FCSTD DOCUMENT  (FreeCAD 0.19R18524 (Git))
Label: footprint-RF-antenna-w-solder-Mask
License: All rights reserved
LicenseURL: http://en.wikipedia.org/wiki/All_rights_reserved
objects: Sketcher::SketchObject×4, App::Annotation×2, App::DocumentObjectGroup×1
note: 4 computed .brp shape members not serialized (recipe doc carries the construction recipe); baked Part::Feature solids carry a one-line shape summary decoded from their .brp

FEATURE [App::Annotation] Text  label="Ref#_1.0mm"
  LabelText = REF**
  Position = (7,5,0)
FEATURE [App::Annotation] Text001  label="Value#_1.0mm"
  LabelText = dimensions not verified 
  Position = (11,3,0)
FEATURE [Sketcher::SketchObject] sSketch  label="Pads_Poly"
  sketch-geometry (82):
    g0: GeomPoint X=3.65001 Y=0 Z=0
    g1: GeomPoint X=3.65001 Y=2.43501 Z=0
    g2: GeomPoint X=3.65001 Y=2.43501 Z=0
    g3: GeomPoint X=3.12901 Y=3.19001 Z=0
    g4: GeomPoint X=3.12901 Y=3.19001 Z=0
    g5: GeomPoint X=0 Y=3.19001 Z=0
    g6: GeomPoint X=0 Y=3.19001 Z=0
    g7: GeomPoint X=0 Y=4.40002 Z=0
    g8: GeomPoint X=0 Y=4.40002 Z=0
    g9: GeomPoint X=1 Y=4.40002 Z=0
    g10: GeomPoint X=1 Y=4.40002 Z=0
    g11: GeomPoint X=1 Y=5.20002 Z=0
    g12: GeomPoint X=1 Y=5.20002 Z=0
    g13: GeomPoint X=-4.80002 Y=5.20002 Z=0
    g14: GeomPoint X=-4.80002 Y=5.20002 Z=0
    g15: GeomPoint X=-4.80002 Y=2.53001 Z=0
    g16: GeomPoint X=-4.80002 Y=2.53001 Z=0
    g17: GeomPoint X=3.20001 Y=2.53001 Z=0
    g18: GeomPoint X=3.20001 Y=2.53001 Z=0
    g19: GeomPoint X=3.20001 Y=0 Z=0
    g20: GeomPoint X=3.20001 Y=0 Z=0
    g21: GeomPoint X=2.20001 Y=0 Z=0
    g22: GeomPoint X=2.20001 Y=0 Z=0
    g23: GeomPoint X=2.20001 Y=1.24 Z=0
    g24: GeomPoint X=2.20001 Y=1.24 Z=0
    g25: GeomPoint X=1 Y=1.24 Z=0
    g26: GeomPoint X=1 Y=1.24 Z=0
    g27: GeomPoint X=1 Y=0 Z=0
    g28: GeomPoint X=1 Y=0 Z=0
    g29: GeomPoint X=0 Y=0 Z=0
    g30: GeomPoint X=0 Y=0 Z=0
    g31: GeomPoint X=0 Y=1.24 Z=0
    g32: GeomPoint X=0 Y=1.24 Z=0
    g33: GeomPoint X=-6.98003 Y=1.24 Z=0
    g34: GeomPoint X=-6.98003 Y=1.24 Z=0
    g35: GeomPoint X=-6.98003 Y=7.41003 Z=0
    g36: GeomPoint X=-6.98003 Y=7.41003 Z=0
    g37: GeomPoint X=18.6001 Y=7.41003 Z=0
    g38: GeomPoint X=18.6001 Y=7.41003 Z=0
    g39: GeomPoint X=18.6001 Y=6.20002 Z=0
    g40: GeomPoint X=18.6001 Y=6.20002 Z=0
    g41: GeomPoint X=2.20001 Y=6.20002 Z=0
    g42: GeomPoint X=2.20001 Y=6.20002 Z=0
    g43: GeomPoint X=2.20001 Y=4.40002 Z=0
    g44: GeomPoint X=2.20001 Y=4.40002 Z=0
    g45: GeomPoint X=3.20001 Y=4.40002 Z=0
    g46: GeomPoint X=3.20001 Y=4.40002 Z=0
    g47: GeomPoint X=3.20001 Y=3.89802 Z=0
    g48: GeomPoint X=3.20001 Y=3.89802 Z=0
    g49: GeomPoint X=4.11002 Y=2.57801 Z=0
    g50: GeomPoint X=4.11002 Y=2.57801 Z=0
    g51: GeomPoint X=4.11002 Y=0 Z=0
    g52: GeomPoint X=4.11002 Y=0 Z=0
    g53: GeomPoint X=3.65001 Y=0 Z=0
    g54: LineSegment StartX=3.65001 StartY=0 StartZ=0 EndX=3.65001 EndY=2.43501 EndZ=0
    g55: LineSegment StartX=3.65001 StartY=2.43501 StartZ=0 EndX=3.12901 EndY=3.19001 EndZ=0
    g56: LineSegment StartX=3.12901 StartY=3.19001 StartZ=0 EndX=-4e-16 EndY=3.19001 EndZ=0
    g57: LineSegment StartX=0 StartY=3.19001 StartZ=0 EndX=0 EndY=4.40002 EndZ=0
    g58: LineSegment StartX=0 StartY=4.40002 StartZ=0 EndX=1 EndY=4.40002 EndZ=0
    g59: LineSegment StartX=1 StartY=4.40002 StartZ=0 EndX=1 EndY=5.20002 EndZ=0
    g60: LineSegment StartX=1 StartY=5.20002 StartZ=0 EndX=-4.80002 EndY=5.20002 EndZ=0
    g61: LineSegment StartX=-4.80002 StartY=5.20002 StartZ=0 EndX=-4.80002 EndY=2.53001 EndZ=0
    g62: LineSegment StartX=-4.80002 StartY=2.53001 StartZ=0 EndX=3.20001 EndY=2.53001 EndZ=0
    g63: LineSegment StartX=3.20001 StartY=2.53001 StartZ=0 EndX=3.20001 EndY=0 EndZ=0
    g64: LineSegment StartX=3.20001 StartY=0 StartZ=0 EndX=2.20001 EndY=0 EndZ=0
    g65: LineSegment StartX=2.20001 StartY=0 StartZ=0 EndX=2.20001 EndY=1.24 EndZ=0
    g66: LineSegment StartX=2.20001 StartY=1.24 StartZ=0 EndX=1 EndY=1.24 EndZ=0
    g67: LineSegment StartX=1 StartY=1.24 StartZ=0 EndX=1 EndY=0 EndZ=0
    g68: LineSegment StartX=1 StartY=0 StartZ=0 EndX=0 EndY=0 EndZ=0
    g69: LineSegment StartX=0 StartY=0 StartZ=0 EndX=0 EndY=1.24 EndZ=0
    g70: LineSegment StartX=0 StartY=1.24 StartZ=0 EndX=-6.98003 EndY=1.24 EndZ=0
    g71: LineSegment StartX=-6.98003 StartY=1.24 StartZ=0 EndX=-6.98003 EndY=7.41003 EndZ=0
    g72: LineSegment StartX=-6.98003 StartY=7.41003 StartZ=0 EndX=18.6001 EndY=7.41003 EndZ=0
    g73: LineSegment StartX=18.6001 StartY=7.41003 StartZ=0 EndX=18.6001 EndY=6.20002 EndZ=0
    g74: LineSegment StartX=18.6001 StartY=6.20002 StartZ=0 EndX=2.20001 EndY=6.20002 EndZ=0
    g75: LineSegment StartX=2.20001 StartY=6.20002 StartZ=0 EndX=2.20001 EndY=4.40002 EndZ=0
    g76: LineSegment StartX=2.20001 StartY=4.40002 StartZ=0 EndX=3.20001 EndY=4.40002 EndZ=0
    g77: LineSegment StartX=3.20001 StartY=4.40002 StartZ=0 EndX=3.20001 EndY=3.89802 EndZ=0
    g78: LineSegment StartX=3.20001 StartY=3.89802 StartZ=0 EndX=4.11002 EndY=2.57801 EndZ=0
    g79: LineSegment StartX=4.11002 StartY=2.57801 StartZ=0 EndX=4.11002 EndY=0 EndZ=0
    g80: LineSegment StartX=4.11002 StartY=0 StartZ=0 EndX=3.65001 EndY=0 EndZ=0
    g81: Circle CenterX=0.52 CenterY=0.25 CenterZ=0 NormalX=0 NormalY=0 NormalZ=1 AngleXU=0 Radius=0.1
  constraints (32):
    c: Vertical(g67)
    c: Coincident(g29,g30)
    c: Coincident(g29,g68)
    c: Coincident(g29,g69)
    c: Coincident(g29,g-1)
    c: DistanceY(g29,g27) = 0
    c: Coincident(g27,g28)
    c: Coincident(g27,g68)
    c: Coincident(g27,g67)
    c: DistanceX(g29,g81) = 0.52
    c: DistanceY(g29,g81) = 0.25
    c: Vertical(g65)
    c: Vertical(g63)
    c: Vertical(g54)
    c: Vertical(g79)
    c: Coincident(g21,g22)
    c: Coincident(g21,g64)
    c: Coincident(g21,g65)
    c: Coincident(g19,g20)
    c: Coincident(g19,g63)
    c: Coincident(g19,g64)
    c: Coincident(g0,g53)
    c: Coincident(g0,g54)
    c: Coincident(g0,g80)
    c: Coincident(g51,g52)
    c: Coincident(g51,g79)
    c: Coincident(g51,g80)
    c: Horizontal(g64)
    c: Horizontal(g80)
    c: DistanceY(g27,g21) = 0
    c: DistanceY(g19,g0) = 0
    c: Radius(g81) = 0.1
FEATURE [Sketcher::SketchObject] sSketch001  label="Pads_TH_SMD"
  sketch-geometry (36):
    g0: GeomPoint X=0 Y=0.500002 Z=0
    g1: GeomPoint X=1 Y=0.500002 Z=0
    g2: GeomPoint X=1 Y=0.500002 Z=0
    g3: GeomPoint X=1 Y=0 Z=0
    g4: GeomPoint X=1 Y=0 Z=0
    g5: GeomPoint X=0 Y=0 Z=0
    g6: GeomPoint X=0 Y=0 Z=0
    g7: GeomPoint X=0 Y=0.500002 Z=0
    g8: GeomPoint X=3.65001 Y=0.500002 Z=0
    g9: GeomPoint X=4.11002 Y=0.500002 Z=0
    g10: GeomPoint X=4.11002 Y=0.500002 Z=0
    g11: GeomPoint X=4.11002 Y=0 Z=0
    g12: GeomPoint X=4.11002 Y=0 Z=0
    g13: GeomPoint X=3.65001 Y=0 Z=0
    g14: GeomPoint X=3.65001 Y=0 Z=0
    g15: GeomPoint X=3.65001 Y=0.500002 Z=0
    g16: GeomPoint X=2.20001 Y=0.500002 Z=0
    g17: GeomPoint X=3.20001 Y=0.500002 Z=0
    g18: GeomPoint X=3.20001 Y=0.500002 Z=0
    g19: GeomPoint X=3.20001 Y=0 Z=0
    g20: GeomPoint X=3.20001 Y=0 Z=0
    g21: GeomPoint X=2.20001 Y=0 Z=0
    g22: GeomPoint X=2.20001 Y=0 Z=0
    g23: GeomPoint X=2.20001 Y=0.500002 Z=0
    g24: LineSegment StartX=0 StartY=0.500002 StartZ=0 EndX=1 EndY=0.500002 EndZ=0
    g25: LineSegment StartX=1 StartY=0.500002 StartZ=0 EndX=1 EndY=0 EndZ=0
    g26: LineSegment StartX=1 StartY=0 StartZ=0 EndX=0 EndY=0 EndZ=0
    g27: LineSegment StartX=0 StartY=0 StartZ=0 EndX=0 EndY=0.500002 EndZ=0
    g28: LineSegment StartX=3.65001 StartY=0.500002 StartZ=0 EndX=4.11002 EndY=0.500002 EndZ=0
    g29: LineSegment StartX=4.11002 StartY=0.500002 StartZ=0 EndX=4.11002 EndY=0 EndZ=0
    g30: LineSegment StartX=4.11002 StartY=0 StartZ=0 EndX=3.65001 EndY=0 EndZ=0
    g31: LineSegment StartX=3.65001 StartY=0 StartZ=0 EndX=3.65001 EndY=0.500002 EndZ=0
    g32: LineSegment StartX=2.20001 StartY=0.500002 StartZ=0 EndX=3.20001 EndY=0.500002 EndZ=0
    g33: LineSegment StartX=3.20001 StartY=0.500002 StartZ=0 EndX=3.20001 EndY=0 EndZ=0
    g34: LineSegment StartX=3.20001 StartY=0 StartZ=0 EndX=2.20001 EndY=0 EndZ=0
    g35: LineSegment StartX=2.20001 StartY=0 StartZ=0 EndX=2.20001 EndY=0.500002 EndZ=0
FEATURE [Sketcher::SketchObject] sSketch002  label="F_Silks_0.16"
  sketch-geometry (9):
    g0: GeomPoint X=-8.1 Y=8.47076 Z=0
    g1: GeomPoint X=19.6114 Y=8.47076 Z=0
    g2: GeomPoint X=19.6114 Y=8.47076 Z=0
    g3: GeomPoint X=-8.1 Y=8.47076 Z=0
    g4: LineSegment StartX=-8.1 StartY=8.47076 StartZ=0 EndX=19.6114 EndY=8.47076 EndZ=0
    g5: LineSegment StartX=19.6114 StartY=8.47076 StartZ=0 EndX=19.6114 EndY=-0.908236 EndZ=0
    g6: LineSegment StartX=3.2107 StartY=-0.908236 StartZ=0 EndX=-8.1 EndY=-0.908236 EndZ=0
    g7: LineSegment StartX=-8.1 StartY=-0.908236 StartZ=0 EndX=-8.1 EndY=8.47076 EndZ=0
    g8: LineSegment StartX=19.6114 StartY=-0.908236 StartZ=0 EndX=4.59639 EndY=-0.908236 EndZ=0
  constraints (15):
    c: Horizontal(g6)
    c: Horizontal(g8)
    c: DistanceY(g7,g7) = 9.379
    c: Coincident(g6,g7)
    c: Vertical(g5)
    c: Coincident(g5,g8)
    c: Coincident(g0,g3)
    c: Coincident(g0,g4)
    c: Coincident(g0,g7)
    c: Coincident(g1,g2)
    c: Coincident(g1,g4)
    c: Coincident(g1,g5)
    c: Vertical(g7)
    c: Equal(g7,g5)
    c: Horizontal(g4)
FEATURE [Sketcher::SketchObject] sSketch003  label="FZ_F_Mask"
  sketch-geometry (12):
    g0: GeomPoint X=-7.45169 Y=7.89363 Z=0
    g1: GeomPoint X=19.0717 Y=7.89363 Z=0
    g2: GeomPoint X=19.0717 Y=7.89363 Z=0
    g3: GeomPoint X=19.0717 Y=-0.323014 Z=0
    g4: GeomPoint X=19.0717 Y=-0.323014 Z=0
    g5: GeomPoint X=-7.45169 Y=-0.323014 Z=0
    g6: GeomPoint X=-7.45169 Y=-0.323014 Z=0
    g7: GeomPoint X=-7.45169 Y=7.89363 Z=0
    g8: LineSegment StartX=-7.45169 StartY=7.89363 StartZ=0 EndX=19.0717 EndY=7.89363 EndZ=0
    g9: LineSegment StartX=19.0717 StartY=7.89363 StartZ=0 EndX=19.0717 EndY=-0.323014 EndZ=0
    g10: LineSegment StartX=19.0717 StartY=-0.323014 StartZ=0 EndX=-7.45169 EndY=-0.323014 EndZ=0
    g11: LineSegment StartX=-7.45169 StartY=-0.323014 StartZ=0 EndX=-7.45169 EndY=7.89363 EndZ=0
FEATURE [App::DocumentObjectGroup] Group  label="fp-template-RF-antenna-poly"
  Group = -> [Text,Text001,sSketch,sSketch001,sSketch002,sSketch003]
